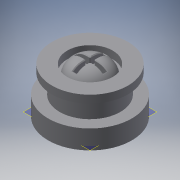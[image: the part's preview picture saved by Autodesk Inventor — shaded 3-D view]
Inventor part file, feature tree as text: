
AUTODESK INVENTOR PART (.ipt)
format: ipt  version: 2017 (Build 210142000, 142)  size: 340,992 bytes
history: native  units: mm
features: sketch x5, extrude x5, chamfer x4, plane x2, reference x2, other x2, fillet x1
ambient origin geometry x8: Origin, YZ Plane, XZ Plane, XY Plane, X Axis, Y Axis, Z Axis, Center Point
bodies: Solid1 (feature_tree)
feature tree (21):
  sketch  "Sketch1"  dims[d0=10.0mm d1=0.0mm d2=6.0mm]
  plane  "Work Plane1"
  extrude  "Extrusion1"  Depth=6.0mm
  extrude  "Extrusion2"  Depth=1.0mm TaperAngle=0.0deg
  plane  "Work Plane2"
  extrude  "Extrusion3"  Depth=11.0mm
  extrude  "Extrusion4"  Depth=5.4mm
  fillet  "Fillet1"  Radius=1.5mm
  extrude  "Extrusion5"  Depth=0.5mm
  chamfer  "Chamfer1"  Distance=4.0mm
  chamfer  "Chamfer2"  Distance=4.0mm
  chamfer  "Chamfer3"  Distance=0.5mm
  chamfer  "Chamfer4"  Distance=1.0mm
  reference  "Reference1"
  reference  "Reference2"
  sketch  "Sketch2"  dims[d3=10.0mm d4=1.0mm d5=0.0mm]
  sketch  "Sketch3"  dims[d6=-1.0mm d7=11.0mm]
  sketch  "Sketch4"  dims[d8=0.5mm d9=2.0mm d10=0.0mm d11=0.0mm d12=5.4mm d13=1.5mm d14=0.0mm]
  sketch  "Sketch5"  dims[d15=2.0mm d16=0.5mm d17=4.0mm d18=4.0mm d19=0.5mm d20=1.0mm d21=0.0mm d22=0.1mm d23=2.0mm d24=45.0deg d25=0.1mm d26=2.0mm d27=45.0deg d28=0.1mm d29=2.0mm d30=45.0deg d31=0.1mm d32=2.0mm d33=45.0deg]
  other  "Assembly1"
  other  "AX12:1"
